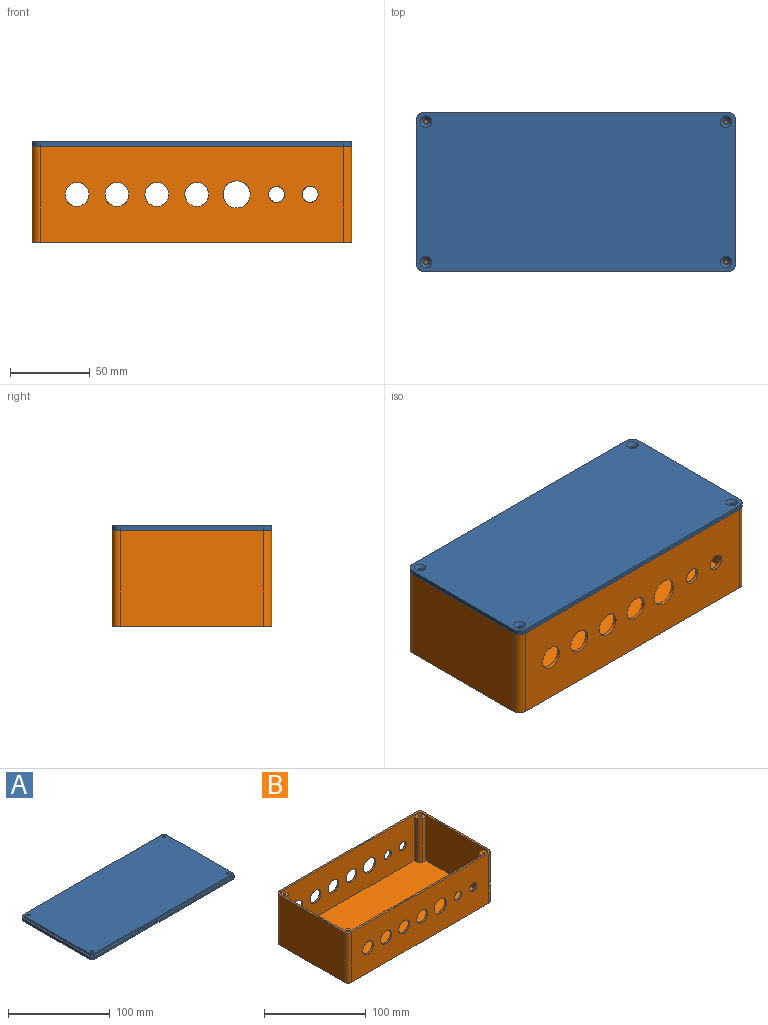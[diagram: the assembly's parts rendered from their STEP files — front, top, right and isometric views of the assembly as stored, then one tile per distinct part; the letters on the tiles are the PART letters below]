
ASSEMBLY  parts=2 mates=1
PART A: 27 faces, bbox 200x100x5 mm
  f0: plane 200x100mm, normal (0,0,1), area 1176.3mm2, adj f1,f2,f3,f4,f6,f7,f8,f9
  f1: plane 90x3mm, normal (-1,0,0), area 270mm2, adj f0,f5,f6,f9
  f2: plane 190x3mm, normal (0,-1,0), area 570mm2, adj f0,f5,f6,f7
  f3: plane 90x3mm, normal (1,0,0), area 270mm2, adj f0,f5,f7,f8
  f4: plane 190x3mm, normal (0,1,0), area 570mm2, adj f0,f5,f8,f9
  f5: plane 200x100mm, normal (0,0,-1), area 19811.1mm2, adj f1,f2,f3,f4,f6,f7,f8,f9
  f6: cylinder r=5mm len=5mm, axis (0,0,1), area 23.6mm2, adj f0,f1,f2,f5
  f7: cylinder r=5mm len=5mm, axis (0,0,-1), area 23.6mm2, adj f0,f2,f3,f5
  f8: cylinder r=5mm len=5mm, axis (0,0,1), area 23.6mm2, adj f0,f3,f4,f5
  f9: cylinder r=5mm len=5mm, axis (0,0,-1), area 23.6mm2, adj f0,f1,f4,f5
  f10: plane 188x2mm, normal (0,1,0), area 376mm2, adj f0,f14,f15,f18
  f11: plane 88x2mm, normal (-1,0,0), area 176mm2, adj f0,f14,f15,f16
  f12: plane 188x2mm, normal (0,-1,0), area 376mm2, adj f0,f14,f16,f17
  f13: plane 88x2mm, normal (1,0,0), area 176mm2, adj f0,f14,f17,f18
  f14: plane 196x96mm, normal (0,0,1), area 18768.1mm2, adj f10,f11,f12,f13,f15,f16,f17,f18
  f15: cylinder r=4mm len=4mm, axis (0,0,1), area 12.6mm2, adj f0,f10,f11,f14
  f16: cylinder r=4mm len=4mm, axis (0,0,-1), area 12.6mm2, adj f0,f11,f12,f14
  f17: cylinder r=4mm len=4mm, axis (0,0,1), area 12.6mm2, adj f0,f12,f13,f14
  f18: cylinder r=4mm len=4mm, axis (0,0,-1), area 12.6mm2, adj f0,f10,f13,f14
  f19: cylinder r=1.65mm len=3.3mm, axis (0,0,1), area 31.1mm2, adj f14,f24
  f20: cylinder r=1.65mm len=3.3mm, axis (0,0,1), area 31.1mm2, adj f14,f23
  f21: cylinder r=1.65mm len=3.3mm, axis (0,0,1), area 31.1mm2, adj f14,f26
  f22: cylinder r=1.65mm len=3.3mm, axis (0,0,1), area 31.1mm2, adj f14,f25
  f23: cone r=3.65mm half-angle=45deg, axis (0,0,-1), area 47.1mm2, adj f5,f20
  f24: cone r=3.65mm half-angle=45deg, axis (0,0,-1), area 47.1mm2, adj f5,f19
  f25: cone r=3.65mm half-angle=45deg, axis (0,0,-1), area 47.1mm2, adj f5,f22
  f26: cone r=3.65mm half-angle=45deg, axis (0,0,-1), area 47.1mm2, adj f5,f21
PART B: 57 faces, bbox 200x100x60 mm
  f0: plane 88x55mm, normal (-1,0,0), area 4416mm2, adj f1,f3,f8,f18,f27,f30,f33,f34
  f1: cylinder r=4mm len=4mm, axis (0,0,-1), area 12.6mm2, adj f0,f6,f8,f34
  f2: plane 188x55mm, normal (0,1,0), area 8825.1mm2, adj f3,f5,f8,f18,f25,f26,f29,f30
  f3: cylinder r=4mm len=4mm, axis (0,0,1), area 12.6mm2, adj f0,f2,f8,f30
  f4: plane 88x55mm, normal (1,0,0), area 4416mm2, adj f5,f7,f8,f18,f19,f22,f24,f26
  f5: cylinder r=4mm len=4mm, axis (0,0,-1), area 12.6mm2, adj f2,f4,f8,f26
  f6: plane 188x55mm, normal (0,-1,0), area 8825.1mm2, adj f1,f7,f8,f18,f21,f22,f31,f34
  f7: cylinder r=4mm len=4mm, axis (0,0,1), area 12.6mm2, adj f4,f6,f8,f22
  f8: plane 200x100mm, normal (0,0,1), area 1176.3mm2, adj f0,f1,f2,f3,f4,f5,f6,f7
  f9: plane 90x60mm, normal (-1,0,0), area 5400mm2, adj f8,f13,f14,f17
  f10: plane 190x60mm, normal (0,-1,0), area 10309.1mm2, adj f8,f13,f14,f15,f50,f51,f52,f53
  f11: plane 90x60mm, normal (1,0,0), area 5400mm2, adj f8,f13,f15,f16
  f12: plane 190x60mm, normal (0,1,0), area 10309.1mm2, adj f8,f13,f16,f17,f43,f44,f45,f46
  f13: plane 200x100mm, normal (0,0,-1), area 19978.5mm2, adj f9,f10,f11,f12,f14,f15,f16,f17
  f14: cylinder r=5mm len=60mm, axis (0,0,1), area 471.2mm2, adj f8,f9,f10,f13
  f15: cylinder r=5mm len=60mm, axis (0,0,-1), area 471.2mm2, adj f8,f10,f11,f13
  f16: cylinder r=5mm len=60mm, axis (0,0,1), area 471.2mm2, adj f8,f11,f12,f13
  f17: cylinder r=5mm len=60mm, axis (0,0,-1), area 471.2mm2, adj f8,f9,f12,f13
  f18: plane 196x96mm, normal (0,0,1), area 18573.7mm2, adj f0,f2,f4,f6,f19,f20,f21,f23
  f19: plane 53x4mm, normal (0,-1,0), area 212mm2, adj f4,f18,f20,f22
  f20: cylinder r=4mm len=53mm, axis (0,0,-1), area 333mm2, adj f18,f19,f21,f22
  f21: plane 53x4mm, normal (1,0,0), area 212mm2, adj f6,f18,f20,f22
  f22: plane 8x8mm, normal (0,0,1), area 52.2mm2, adj f4,f6,f7,f19,f20,f21,f41
  f23: cylinder r=4mm len=53mm, axis (0,0,-1), area 333mm2, adj f18,f24,f25,f26
  f24: plane 53x4mm, normal (0,1,0), area 212mm2, adj f4,f18,f23,f26
  f25: plane 53x4mm, normal (1,0,0), area 212mm2, adj f2,f18,f23,f26
  f26: plane 8x8mm, normal (0,0,1), area 52.2mm2, adj f2,f4,f5,f23,f24,f25,f39
  f27: plane 53x4mm, normal (0,1,0), area 212mm2, adj f0,f18,f28,f30
  f28: cylinder r=4mm len=53mm, axis (0,0,-1), area 333mm2, adj f18,f27,f29,f30
  f29: plane 53x4mm, normal (-1,0,0), area 212mm2, adj f2,f18,f28,f30
  f30: plane 8x8mm, normal (0,0,1), area 52.2mm2, adj f0,f2,f3,f27,f28,f29,f37
  f31: plane 53x4mm, normal (-1,0,0), area 212mm2, adj f6,f18,f32,f34
  f32: cylinder r=4mm len=53mm, axis (0,0,-1), area 333mm2, adj f18,f31,f33,f34
  f33: plane 53x4mm, normal (0,-1,0), area 212mm2, adj f0,f18,f32,f34
  f34: plane 8x8mm, normal (0,0,1), area 52.2mm2, adj f0,f1,f6,f31,f32,f33,f35
  f35: cylinder r=1.25mm len=40mm, axis (0,0,1), area 314.2mm2, adj f34,f36
  f36: plane 2.5x2.5mm, normal (0,0,1), area 4.9mm2, adj f35
  f37: cylinder r=1.25mm len=40mm, axis (0,0,1), area 314.2mm2, adj f30,f38
  f38: plane 2.5x2.5mm, normal (0,0,1), area 4.9mm2, adj f37
  f39: cylinder r=1.25mm len=40mm, axis (0,0,1), area 314.2mm2, adj f26,f40
  f40: plane 2.5x2.5mm, normal (0,0,1), area 4.9mm2, adj f39
  f41: cylinder r=1.25mm len=40mm, axis (0,0,1), area 314.2mm2, adj f22,f42
  f42: plane 2.5x2.5mm, normal (0,0,1), area 4.9mm2, adj f41
  f43: cylinder r=5mm len=10mm, axis (0,-1,0), area 62.8mm2, adj f6,f12
  f44: cylinder r=5mm len=10mm, axis (0,-1,0), area 62.8mm2, adj f6,f12
  f45: cylinder r=8.5mm len=17mm, axis (0,-1,0), area 106.8mm2, adj f6,f12
  f46: cylinder r=7.5mm len=15mm, axis (0,-1,0), area 94.2mm2, adj f6,f12
  f47: cylinder r=7.5mm len=15mm, axis (0,-1,0), area 94.2mm2, adj f6,f12
  f48: cylinder r=7.5mm len=15mm, axis (0,-1,0), area 94.2mm2, adj f6,f12
  f49: cylinder r=7.5mm len=15mm, axis (0,-1,0), area 94.2mm2, adj f6,f12
  f50: cylinder r=5mm len=10mm, axis (0,-1,0), area 62.8mm2, adj f2,f10
  f51: cylinder r=5mm len=10mm, axis (0,-1,0), area 62.8mm2, adj f2,f10
  f52: cylinder r=8.5mm len=17mm, axis (0,-1,0), area 106.8mm2, adj f2,f10
  f53: cylinder r=7.5mm len=15mm, axis (0,-1,0), area 94.2mm2, adj f2,f10
  f54: cylinder r=7.5mm len=15mm, axis (0,-1,0), area 94.2mm2, adj f2,f10
  f55: cylinder r=7.5mm len=15mm, axis (0,-1,0), area 94.2mm2, adj f2,f10
  f56: cylinder r=7.5mm len=15mm, axis (0,-1,0), area 94.2mm2, adj f2,f10
PLACE A rot(axis=(1,0,0),180deg) t=(0,100,63)mm
PLACE B at identity
MATE planar A.f9 <-> B.f8  axis (0,0,-1) through (5,5,60)mm
